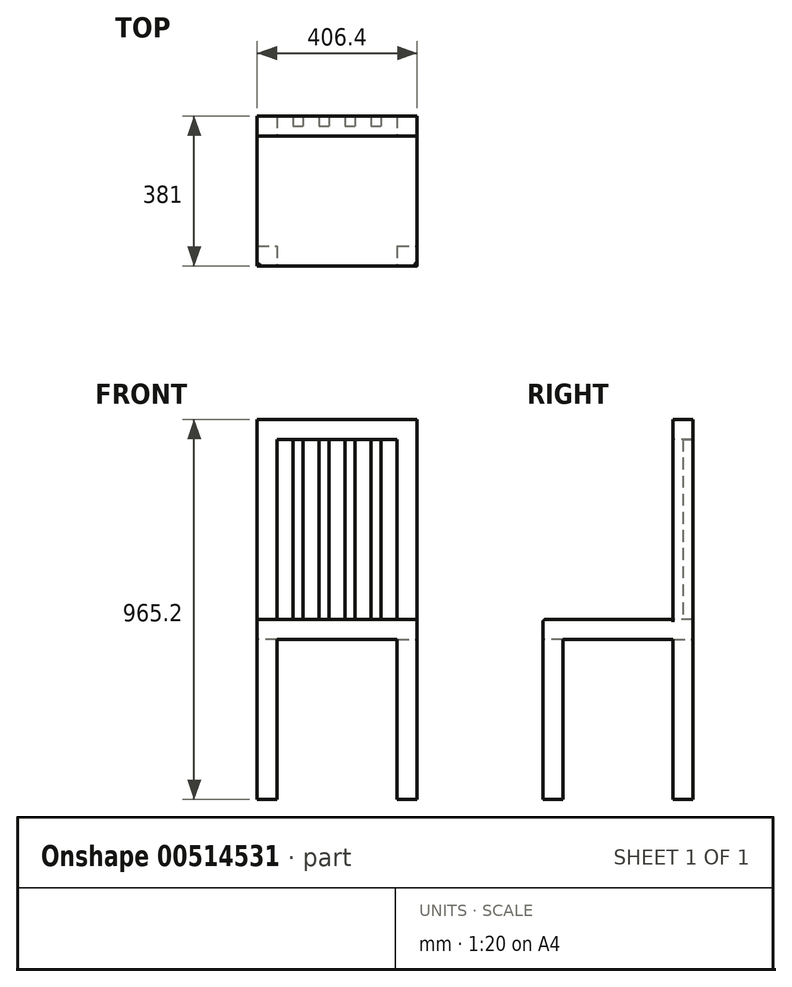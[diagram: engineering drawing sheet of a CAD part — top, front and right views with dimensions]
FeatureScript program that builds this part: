
annotation { "Feature Type Name" : "Feature", "Feature Type Description" : "" }
export const myFeature = defineFeature(function(context is Context, id is Id, definition is map)
    precondition{}
    {
        {
            var Q0;
            Q0=qCreatedBy(makeId("Top.planeOp"),FACE);
            var sketch = newSketch(context, id + "F0", { "sketchPlane" : qUnion([Q0])});
            skLineSegment(sketch, "E0.bottom", {"start": v(0, 0) * mm, "end": v(-50.8, 0) * mm});
            skLineSegment(sketch, "E0.top", {"start": v(0, 50.8) * mm, "end": v(-50.8, 50.8) * mm});
            skLineSegment(sketch, "E0.left", {"start": v(0, 0) * mm, "end": v(0, 50.8) * mm});
            skLineSegment(sketch, "E0.right", {"start": v(-50.8, 0) * mm, "end": v(-50.8, 50.8) * mm});
            skLineSegment(sketch, "E1.bottom", {"start": v(304.8, 50.8) * mm, "end": v(355.6, 50.8) * mm});
            skLineSegment(sketch, "E1.top", {"start": v(304.8, 0) * mm, "end": v(355.6, 0) * mm});
            skLineSegment(sketch, "E1.left", {"start": v(304.8, 50.8) * mm, "end": v(304.8, 0) * mm});
            skLineSegment(sketch, "E1.right", {"start": v(355.6, 50.8) * mm, "end": v(355.6, 0) * mm});
            skLineSegment(sketch, "E2.bottom", {"start": v(304.8, -279.4) * mm, "end": v(355.6, -279.4) * mm});
            skLineSegment(sketch, "E2.top", {"start": v(304.8, -330.2) * mm, "end": v(355.6, -330.2) * mm});
            skLineSegment(sketch, "E2.left", {"start": v(304.8, -279.4) * mm, "end": v(304.8, -330.2) * mm});
            skLineSegment(sketch, "E2.right", {"start": v(355.6, -279.4) * mm, "end": v(355.6, -330.2) * mm});
            skLineSegment(sketch, "E3.bottom", {"start": v(-50.8, -279.4) * mm, "end": v(0, -279.4) * mm});
            skLineSegment(sketch, "E3.top", {"start": v(-50.8, -330.2) * mm, "end": v(0, -330.2) * mm});
            skLineSegment(sketch, "E3.left", {"start": v(-50.8, -279.4) * mm, "end": v(-50.8, -330.2) * mm});
            skLineSegment(sketch, "E3.right", {"start": v(0, -279.4) * mm, "end": v(0, -330.2) * mm});
            skSolve(sketch);
        }
        {
            var Q0;
            Q0 = qSketchRegion(id + "F0", true);
            extrude(context, id + "F1", {"entities" : qUnion([Q0]), "depth" : 406.4 * mm, "offsetDistance" : 25.4 * mm});
        }
        {
            var Q0;
            Q0=makeQuery(id+"F1.opExtrude","CAP_FACE",FACE,{"disambiguationData":[OSD([sQuery(id+"F0.wireOp",EDGE,"E1.bottom"),sQuery(id+"F0.wireOp",EDGE,"E1.top"),sQuery(id+"F0.wireOp",EDGE,"E1.left"),sQuery(id+"F0.wireOp",EDGE,"E1.right")])],"isStart":false});
            var sketch = newSketch(context, id + "F2", { "sketchPlane" : qUnion([Q0])});
            skLineSegment(sketch, "E4.bottom", {"start": v(355.6, 50.8) * mm, "end": v(-50.8, 50.8) * mm});
            skLineSegment(sketch, "E4.top", {"start": v(355.6, -330.2) * mm, "end": v(-50.8, -330.2) * mm});
            skLineSegment(sketch, "E4.left", {"start": v(355.6, 50.8) * mm, "end": v(355.6, -330.2) * mm});
            skLineSegment(sketch, "E4.right", {"start": v(-50.8, 50.8) * mm, "end": v(-50.8, -330.2) * mm});
            skSolve(sketch);
        }
        {
            var Q0;
            {var subQ2=sQuery(id+"F2.wireOp",EDGE,"E4.top");Q0=makeQuery(id+"F2.imprint","IMPRINT",FACE,{"disambiguationData":[TD([[makeQuery(id+"F2.imprint","IMPRINT",EDGE,{"derivedFrom":subQ2}),-1.0]])]});}
            var Q1;
            {var subQ4=makeQuery(id+"F1.opExtrude","CAP_EDGE",EDGE,{"disambiguationData":[OSD([sQuery(id+"F0.wireOp",EDGE,"E1.top")])],"isStart":false});Q1=makeQuery(id+"F2.imprint","IMPRINT",FACE,{"disambiguationData":[TD([[makeQuery(id+"F2.imprint","IMPRINT",EDGE,{"derivedFrom":subQ4}),1.0]])]});}
            extrude(context, id + "F3", {"entities" : qUnion([Q0, Q1]), "operationType" : NewBodyOperationType.ADD, "depth" : 50.8 * mm, "offsetDistance" : 25.4 * mm});
        }
        {
            var Q0;
            Q0=makeQuery(id+"F3.opExtrude","CAP_FACE",FACE,{"disambiguationData":[OSD([sQuery(id+"F2.wireOp",EDGE,"E4.bottom"),sQuery(id+"F2.wireOp",EDGE,"E4.top"),sQuery(id+"F2.wireOp",EDGE,"E4.left"),sQuery(id+"F2.wireOp",EDGE,"E4.right")])],"isStart":false});
            var sketch = newSketch(context, id + "F4", { "sketchPlane" : qUnion([Q0])});
            skLineSegment(sketch, "E5.bottom", {"start": v(-50.8, 50.8) * mm, "end": v(0, 50.8) * mm});
            skLineSegment(sketch, "E5.top", {"start": v(-50.8, 0) * mm, "end": v(0, 0) * mm});
            skLineSegment(sketch, "E5.left", {"start": v(-50.8, 50.8) * mm, "end": v(-50.8, 0) * mm});
            skLineSegment(sketch, "E5.right", {"start": v(0, 50.8) * mm, "end": v(0, 0) * mm});
            skLineSegment(sketch, "E6.bottom", {"start": v(40.64, 50.8) * mm, "end": v(66.04, 50.8) * mm});
            skLineSegment(sketch, "E6.top", {"start": v(40.64, 25.4) * mm, "end": v(66.04, 25.4) * mm});
            skLineSegment(sketch, "E6.left", {"start": v(40.64, 50.8) * mm, "end": v(40.64, 25.4) * mm});
            skLineSegment(sketch, "E6.right", {"start": v(66.04, 50.8) * mm, "end": v(66.04, 25.4) * mm});
            skLineSegment(sketch, "E7.bottom", {"start": v(106.68, 50.8) * mm, "end": v(132.08, 50.8) * mm});
            skLineSegment(sketch, "E7.top", {"start": v(106.68, 25.4) * mm, "end": v(132.08, 25.4) * mm});
            skLineSegment(sketch, "E7.left", {"start": v(106.68, 50.8) * mm, "end": v(106.68, 25.4) * mm});
            skLineSegment(sketch, "E7.right", {"start": v(132.08, 50.8) * mm, "end": v(132.08, 25.4) * mm});
            skLineSegment(sketch, "E8.bottom", {"start": v(172.72, 50.8) * mm, "end": v(198.12, 50.8) * mm});
            skLineSegment(sketch, "E8.top", {"start": v(172.72, 25.4) * mm, "end": v(198.12, 25.4) * mm});
            skLineSegment(sketch, "E8.left", {"start": v(172.72, 50.8) * mm, "end": v(172.72, 25.4) * mm});
            skLineSegment(sketch, "E8.right", {"start": v(198.12, 50.8) * mm, "end": v(198.12, 25.4) * mm});
            skLineSegment(sketch, "E9.bottom", {"start": v(238.76, 50.8) * mm, "end": v(264.16, 50.8) * mm});
            skLineSegment(sketch, "E9.top", {"start": v(238.76, 25.4) * mm, "end": v(264.16, 25.4) * mm});
            skLineSegment(sketch, "E9.left", {"start": v(238.76, 50.8) * mm, "end": v(238.76, 25.4) * mm});
            skLineSegment(sketch, "E9.right", {"start": v(264.16, 50.8) * mm, "end": v(264.16, 25.4) * mm});
            skLineSegment(sketch, "E10.bottom", {"start": v(355.6, 50.8) * mm, "end": v(304.8, 50.8) * mm});
            skLineSegment(sketch, "E10.top", {"start": v(355.6, 0) * mm, "end": v(304.8, 0) * mm});
            skLineSegment(sketch, "E10.left", {"start": v(355.6, 50.8) * mm, "end": v(355.6, 0) * mm});
            skLineSegment(sketch, "E10.right", {"start": v(304.8, 50.8) * mm, "end": v(304.8, 0) * mm});
            skLineSegment(sketch, "E11", {"start": v(0, 50.8) * mm, "end": v(40.64, 50.8) * mm});
            skLineSegment(sketch, "E12", {"start": v(66.04, 50.8) * mm, "end": v(106.68, 50.8) * mm});
            skLineSegment(sketch, "E13", {"start": v(132.08, 50.8) * mm, "end": v(172.72, 50.8) * mm});
            skLineSegment(sketch, "E14", {"start": v(198.12, 50.8) * mm, "end": v(238.76, 50.8) * mm});
            skLineSegment(sketch, "E15", {"start": v(264.16, 50.8) * mm, "end": v(304.8, 50.8) * mm});
            skSolve(sketch);
        }
        {
            var Q0;
            Q0=makeQuery(id+"F4.imprint","IMPRINT",FACE,{"disambiguationData":[TD([[makeQuery(id+"F4.imprint","IMPRINT",EDGE,{"derivedFrom":sQuery(id+"F4.wireOp",EDGE,"E5.bottom")}),1.0]])]});
            var Q1;
            Q1=makeQuery(id+"F4.imprint","IMPRINT",FACE,{"disambiguationData":[TD([[makeQuery(id+"F4.imprint","IMPRINT",EDGE,{"derivedFrom":sQuery(id+"F4.wireOp",EDGE,"E6.bottom")}),1.0]])]});
            var Q2;
            Q2=makeQuery(id+"F4.imprint","IMPRINT",FACE,{"disambiguationData":[TD([[makeQuery(id+"F4.imprint","IMPRINT",EDGE,{"derivedFrom":sQuery(id+"F4.wireOp",EDGE,"E7.bottom")}),1.0]])]});
            var Q3;
            Q3=makeQuery(id+"F4.imprint","IMPRINT",FACE,{"disambiguationData":[TD([[makeQuery(id+"F4.imprint","IMPRINT",EDGE,{"derivedFrom":sQuery(id+"F4.wireOp",EDGE,"E8.bottom")}),1.0]])]});
            var Q4;
            Q4=makeQuery(id+"F4.imprint","IMPRINT",FACE,{"disambiguationData":[TD([[makeQuery(id+"F4.imprint","IMPRINT",EDGE,{"derivedFrom":sQuery(id+"F4.wireOp",EDGE,"E9.bottom")}),1.0]])]});
            var Q5;
            Q5=makeQuery(id+"F4.imprint","IMPRINT",FACE,{"disambiguationData":[TD([[makeQuery(id+"F4.imprint","IMPRINT",EDGE,{"derivedFrom":sQuery(id+"F4.wireOp",EDGE,"E10.bottom")}),1.0]])]});
            extrude(context, id + "F5", {"entities" : qUnion([Q0, Q1, Q2, Q3, Q4, Q5]), "operationType" : NewBodyOperationType.ADD, "depth" : 508 * mm, "offsetDistance" : 25.4 * mm});
        }
        {
            var Q0;
            Q0=makeQuery(id+"F5.opExtrude","SWEPT_FACE",FACE,{"disambiguationData":[OSD([sQuery(id+"F4.wireOp",EDGE,"E5.right")])]});
            var sketch = newSketch(context, id + "F6", { "sketchPlane" : qUnion([Q0])});
            skLineSegment(sketch, "E16.bottom", {"start": v(50.8, 965.2) * mm, "end": v(0, 965.2) * mm});
            skLineSegment(sketch, "E16.top", {"start": v(50.8, 914.4) * mm, "end": v(0, 914.4) * mm});
            skLineSegment(sketch, "E16.left", {"start": v(50.8, 965.2) * mm, "end": v(50.8, 914.4) * mm});
            skLineSegment(sketch, "E16.right", {"start": v(0, 965.2) * mm, "end": v(0, 914.4) * mm});
            skSolve(sketch);
        }
        {
            var Q0;
            Q0=makeQuery(id+"F6.imprint","IMPRINT",FACE,{"disambiguationData":[TD([[makeQuery(id+"F6.imprint","IMPRINT",EDGE,{"derivedFrom":sQuery(id+"F6.wireOp",EDGE,"E16.bottom")}),1.0]])]});
            extrude(context, id + "F7", {"entities" : qUnion([Q0]), "operationType" : NewBodyOperationType.ADD, "depth" : 355.6 * mm, "offsetDistance" : 25.4 * mm});
        }
        {
            var Q0;
            Q0=makeQuery(id+"F3.opExtrude","CAP_EDGE",EDGE,{"disambiguationData":[OSD([sQuery(id+"F2.wireOp",EDGE,"E4.right")])],"isStart":false});
            var Q1;
            Q1=makeQuery(id+"F3.opExtrude","CAP_EDGE",EDGE,{"disambiguationData":[OSD([sQuery(id+"F2.wireOp",EDGE,"E4.top")])],"isStart":false});
            var Q2;
            Q2=makeQuery(id+"F3.opExtrude","CAP_EDGE",EDGE,{"disambiguationData":[OSD([sQuery(id+"F2.wireOp",EDGE,"E4.left")])],"isStart":false});
            fillet(context, id + "F8", {"entities" : qUnion([Q0, Q1, Q2]), "radius" : 6.35 * mm, "tangentPropagation" : true, "allowEdgeOverflow" : false});
        }
    });
